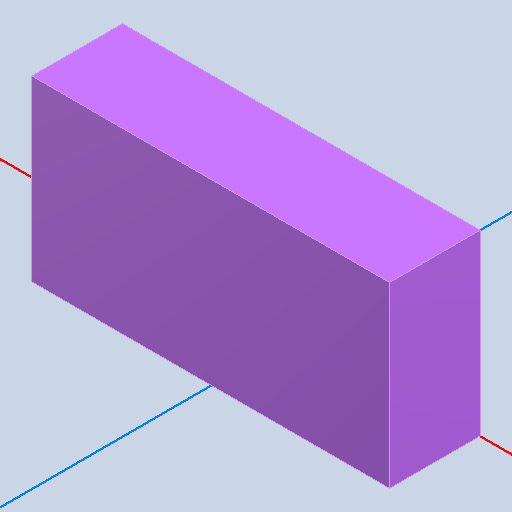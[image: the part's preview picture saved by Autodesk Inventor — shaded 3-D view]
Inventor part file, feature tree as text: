
AUTODESK INVENTOR PART (.ipt)
format: ipt  version: 2022 (Build 260153000, 153)  size: 91,648 bytes
history: native  units: mm
features: other x2, extrude x1
ambient origin geometry x8: Origin, YZ Plane, XZ Plane, XY Plane, X Axis, Y Axis, Z Axis, Center Point
bodies: Body1 (feature_tree)
feature tree (3):
  other  "Твердое тело1"
  extrude  "Выдавливание1"  Depth=1.0mm TaperAngle=0.0deg
  other  "R0805, R0805_23"
